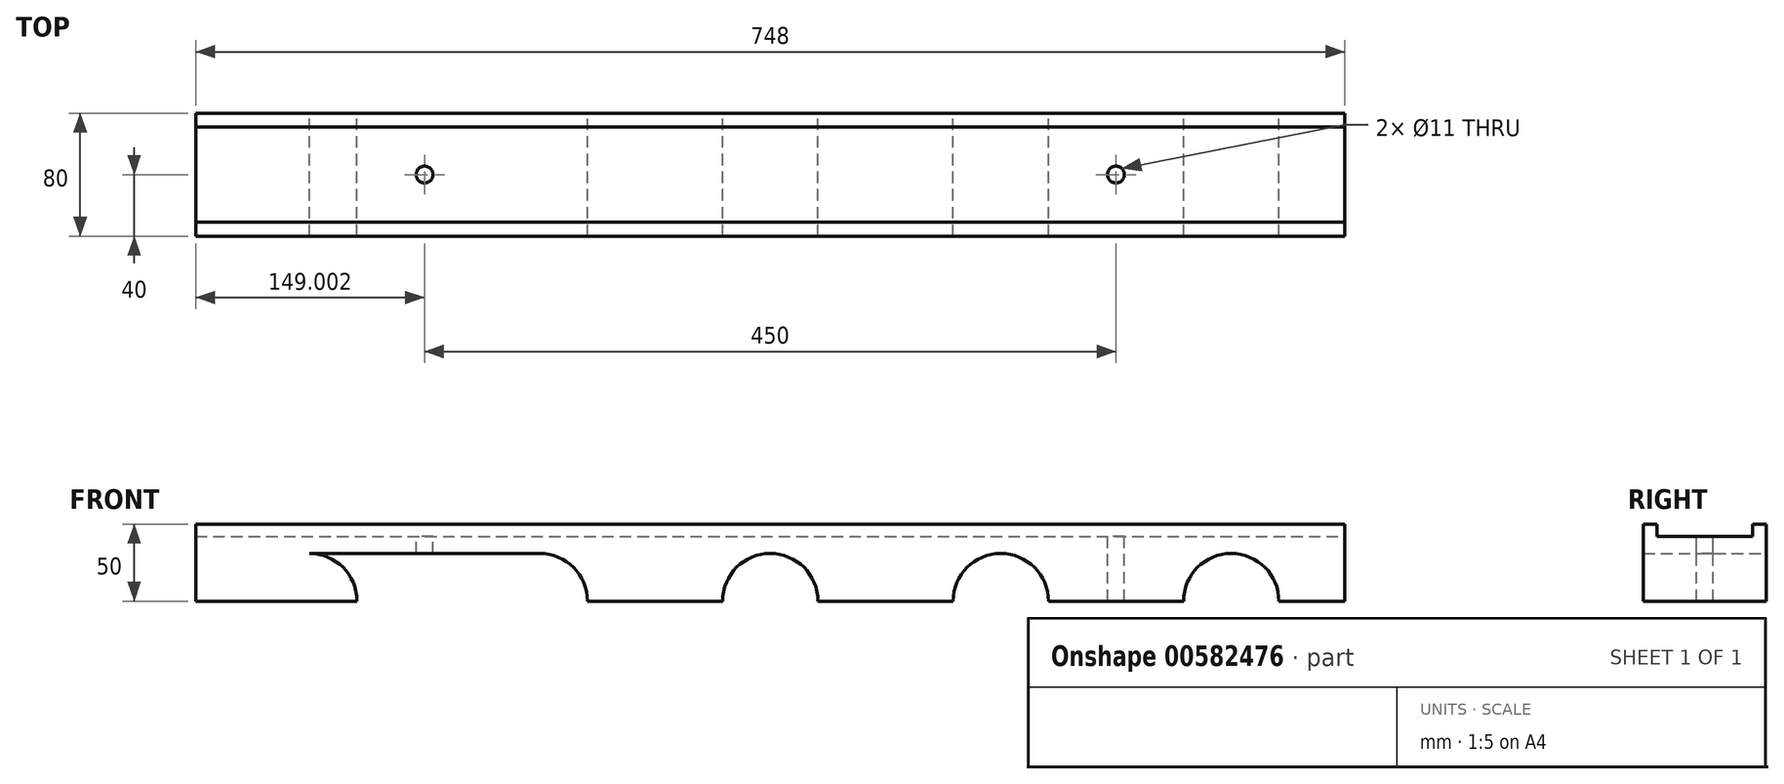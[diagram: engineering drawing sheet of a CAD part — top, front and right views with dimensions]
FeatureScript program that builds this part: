
annotation { "Feature Type Name" : "Feature", "Feature Type Description" : "" }
export const myFeature = defineFeature(function(context is Context, id is Id, definition is map)
    precondition{}
    {
        {
            var Q0;
            Q0=qCreatedBy(makeId("Front.planeOp"),FACE);
            var sketch = newSketch(context, id + "F0", { "sketchPlane" : qUnion([Q0])});
            skLineSegment(sketch, "E0.bottom", {"start": v(-211.94, 106.33) * mm, "end": v(536.06, 106.33) * mm});
            skLineSegment(sketch, "E0.top", {"start": v(-211.94, 56.33) * mm, "end": v(536.06, 56.33) * mm});
            skLineSegment(sketch, "E0.left", {"start": v(-211.94, 106.33) * mm, "end": v(-211.94, 56.33) * mm});
            skLineSegment(sketch, "E0.right", {"start": v(536.06, 106.33) * mm, "end": v(536.06, 56.33) * mm});
            skArc(sketch, "E1", {"start": v(-106.94, 56.33) * mm, "mid": v(-137.94, 87.33) * mm, "end": v(-168.94, 56.33) * mm});
            skArc(sketch, "E2", {"start": v(193.06, 56.33) * mm, "mid": v(162.06, 87.33) * mm, "end": v(131.06, 56.33) * mm});
            skArc(sketch, "E3", {"start": v(493.06, 56.33) * mm, "mid": v(462.06, 87.33) * mm, "end": v(431.06, 56.33) * mm});
            skLineSegment(sketch, "E4", {"start": v(-211.94, 87.33) * mm, "end": v(536.06, 87.33) * mm});
            skArc(sketch, "E5", {"start": v(43.06, 56.33) * mm, "mid": v(12.06, 87.33) * mm, "end": v(-18.94, 56.33) * mm});
            skArc(sketch, "E6", {"start": v(343.06, 56.33) * mm, "mid": v(312.06, 87.33) * mm, "end": v(281.06, 56.33) * mm});
            skLineSegment(sketch, "E7", {"start": v(536.06, 98.33) * mm, "end": v(-211.94, 98.33) * mm});
            skSolve(sketch);
        }
        {
            var Q0;
            {var subQ0=sQuery(id+"F0.wireOp",EDGE,"E0.left");var subQ1=sQuery(id+"F0.wireOp",EDGE,"E0.top");var subQ2=makeQuery(id+"F0.imprint","INTERSECT",VERTEX,{"derivedFrom":[subQ1,subQ0]});Q0=makeQuery(id+"F0.imprint","IMPRINT",FACE,{"disambiguationData":[TD([[makeQuery(id+"F0.imprint","IMPRINT",EDGE,{"disambiguationData":[TD([[subQ2,-1.0]])],"derivedFrom":subQ1}),1.0]])]});}
            var Q1;
            {var subQ0=sQuery(id+"F0.wireOp",EDGE,"E1");var subQ1=sQuery(id+"F0.wireOp",EDGE,"E0.top");var subQ2=makeQuery(id+"F0.imprint","INTERSECT",VERTEX,{"disambiguationData":[OD(0.0)],"derivedFrom":[subQ1,subQ0]});Q1=makeQuery(id+"F0.imprint","IMPRINT",FACE,{"disambiguationData":[TD([[makeQuery(id+"F0.imprint","IMPRINT",EDGE,{"disambiguationData":[TD([[subQ2,-1.0]])],"derivedFrom":subQ1}),1.0]])]});}
            var Q2;
            {var subQ0=sQuery(id+"F0.wireOp",EDGE,"E2");var subQ1=sQuery(id+"F0.wireOp",EDGE,"E0.top");var subQ2=makeQuery(id+"F0.imprint","INTERSECT",VERTEX,{"disambiguationData":[OD(1.0)],"derivedFrom":[subQ1,subQ0]});Q2=makeQuery(id+"F0.imprint","IMPRINT",FACE,{"disambiguationData":[TD([[makeQuery(id+"F0.imprint","IMPRINT",EDGE,{"disambiguationData":[TD([[subQ2,1.0]])],"derivedFrom":subQ1}),1.0]])]});}
            var Q3;
            {var subQ0=sQuery(id+"F0.wireOp",EDGE,"E2");var subQ1=sQuery(id+"F0.wireOp",EDGE,"E0.top");var subQ2=makeQuery(id+"F0.imprint","INTERSECT",VERTEX,{"disambiguationData":[OD(0.0)],"derivedFrom":[subQ1,subQ0]});Q3=makeQuery(id+"F0.imprint","IMPRINT",FACE,{"disambiguationData":[TD([[makeQuery(id+"F0.imprint","IMPRINT",EDGE,{"disambiguationData":[TD([[subQ2,-1.0]])],"derivedFrom":subQ1}),1.0]])]});}
            var Q4;
            {var subQ0=sQuery(id+"F0.wireOp",EDGE,"E3");var subQ1=sQuery(id+"F0.wireOp",EDGE,"E0.top");var subQ2=makeQuery(id+"F0.imprint","INTERSECT",VERTEX,{"disambiguationData":[OD(1.0)],"derivedFrom":[subQ1,subQ0]});Q4=makeQuery(id+"F0.imprint","IMPRINT",FACE,{"disambiguationData":[TD([[makeQuery(id+"F0.imprint","IMPRINT",EDGE,{"disambiguationData":[TD([[subQ2,1.0]])],"derivedFrom":subQ1}),1.0]])]});}
            var Q5;
            {var subQ0=sQuery(id+"F0.wireOp",EDGE,"E0.right");var subQ1=sQuery(id+"F0.wireOp",EDGE,"E0.top");var subQ2=makeQuery(id+"F0.imprint","INTERSECT",VERTEX,{"derivedFrom":[subQ1,subQ0]});Q5=makeQuery(id+"F0.imprint","IMPRINT",FACE,{"disambiguationData":[TD([[makeQuery(id+"F0.imprint","IMPRINT",EDGE,{"disambiguationData":[TD([[subQ2,1.0]])],"derivedFrom":subQ1}),1.0]])]});}
            var Q6;
            {var subQ5=sQuery(id+"F0.wireOp",EDGE,"E7");Q6=makeQuery(id+"F0.imprint","IMPRINT",FACE,{"disambiguationData":[TD([[makeQuery(id+"F0.imprint","IMPRINT",EDGE,{"derivedFrom":subQ5}),1.0]])]});}
            extrude(context, id + "F1", {"entities" : qUnion([Q0, Q1, Q2, Q3, Q4, Q5, Q6]), "depth" : 80 * mm, "offsetDistance" : 25 * mm});
        }
        {
            var Q0;
            Q0=makeQuery(id+"F1.opExtrude","SWEPT_FACE",FACE,{"disambiguationData":[OSD([sQuery(id+"F0.wireOp",EDGE,"E0.right")])]});
            var sketch = newSketch(context, id + "F2", { "sketchPlane" : qUnion([Q0])});
            skLineSegment(sketch, "E8", {"start": v(-80, 98.33) * mm, "end": v(-80, 106.33) * mm});
            skLineSegment(sketch, "E9", {"start": v(-80, 106.33) * mm, "end": v(-71, 106.33) * mm});
            skLineSegment(sketch, "E10", {"start": v(-71, 106.33) * mm, "end": v(-71, 98.33) * mm});
            skLineSegment(sketch, "E11", {"start": v(0, 98.33) * mm, "end": v(0, 106.33) * mm});
            skLineSegment(sketch, "E12", {"start": v(0, 106.33) * mm, "end": v(-9, 106.33) * mm});
            skLineSegment(sketch, "E13", {"start": v(-9, 106.33) * mm, "end": v(-9, 98.33) * mm});
            skSolve(sketch);
        }
        {
            var Q0;
            {var subQ0=sQuery(id+"F2.wireOp",EDGE,"E8");Q0=makeQuery(id+"F2.imprint","IMPRINT",FACE,{"disambiguationData":[TD([[makeQuery(id+"F2.imprint","IMPRINT",EDGE,{"derivedFrom":subQ0}),-1.0]])]});}
            var Q1;
            {var subQ0=sQuery(id+"F2.wireOp",EDGE,"E11");Q1=makeQuery(id+"F2.imprint","IMPRINT",FACE,{"disambiguationData":[TD([[makeQuery(id+"F2.imprint","IMPRINT",EDGE,{"derivedFrom":subQ0}),1.0]])]});}
            extrude(context, id + "F3", {"entities" : qUnion([Q0, Q1]), "operationType" : NewBodyOperationType.ADD, "oppositeDirection" : true, "depth" : 748 * mm, "offsetDistance" : 25 * mm});
        }
        {
            var Q0;
            Q0=makeQuery(id+"F1.opExtrude","SWEPT_FACE",FACE,{"disambiguationData":[OSD([sQuery(id+"F0.wireOp",EDGE,"E7")])]});
            var sketch = newSketch(context, id + "F4", { "sketchPlane" : qUnion([Q0])});
            skCircle(sketch, "E14", {"center": v(387.06, -40) * mm, "radius": 5.5 * mm});
            skCircle(sketch, "E15", {"center": v(-62.94, -40) * mm, "radius": 5.5 * mm});
            skSolve(sketch);
        }
        {
            var Q0;
            Q0=makeQuery(id+"F4.imprint","IMPRINT",FACE,{"disambiguationData":[TD([[makeQuery(id+"F4.imprint","IMPRINT",EDGE,{"derivedFrom":sQuery(id+"F4.wireOp",EDGE,"E14")}),1.0]])]});
            var Q1;
            Q1=makeQuery(id+"F4.imprint","IMPRINT",FACE,{"disambiguationData":[TD([[makeQuery(id+"F4.imprint","IMPRINT",EDGE,{"derivedFrom":sQuery(id+"F4.wireOp",EDGE,"E15")}),1.0]])]});
            extrude(context, id + "F5", {"entities" : qUnion([Q0, Q1]), "operationType" : NewBodyOperationType.REMOVE, "oppositeDirection" : true, "depth" : 42 * mm, "offsetDistance" : 25 * mm});
        }
    });
